# Revit family: 208_5cc59a5770094b1e904d8fad437c5c
name_source: partatom
category: Air Terminals
units: mm (PartAtom-declared; Revit-internal decimal feet)

## family parameters
Always vertical = Yes
Cut with Voids When Loaded = No
Part Type = Normal
Room Calculation Point = Yes
Round Connector Dimension = Use Diameter
Shared = No
Work Plane-Based = No

## types (1)
- 100-02345
    CLBTZ = 0 mm  [stored 0 ft]
    CL_Location_5000 = 5000 mm  [stored 16.4042 ft]
    D = 100 mm
    DT2 = 50 mm  [stored 0.164042 ft]
    Description = Cowel male steel
    H1 = 90 mm
    HT2 = 97 mm
    H_ARR = 0 mm  [stored 0 ft]
    L = 70 mm  [stored 0.229659 ft]
    L_ARR = 400 mm  [stored 1.31234 ft]
    MC Product Code = 100-02345
    Manufacturer = Flexit
    QmdConnectorList = 201;D
    W1 = 112 mm  [stored 0.367454 ft]
    W1T2 = 56 mm  [stored 0.183727 ft]
    W2 = 147 mm  [stored 0.482283 ft]
    W2T2 = 74 mm
    W_ARR = 400 mm  [stored 1.31234 ft]
    X = 75 mm  [stored 0.246063 ft]
    magiPartTypeId = 208
    magiProductFamilyId = 5cc59a5770094b1e904d8fad437c5c
    magiProductId = 5f233db9159041f3909604f1c1fe92

note: [stored X ft] marks values corroborated as IEEE doubles in the binary element streams (Revit-internal decimal feet)

## geometry (parser evidence)
native form markers: Sweep x2
no freeform markers — native parametric forms only
